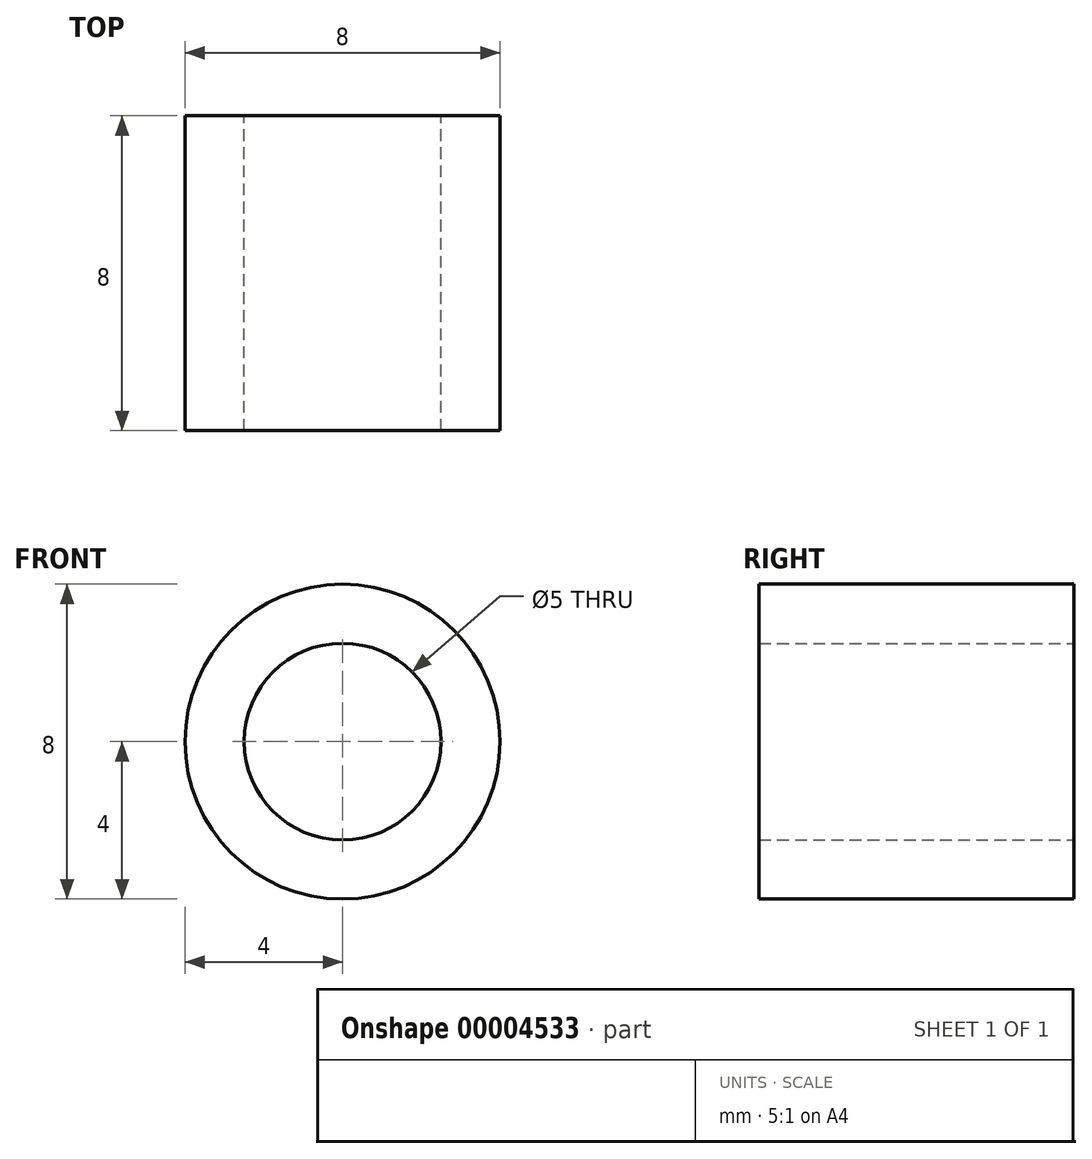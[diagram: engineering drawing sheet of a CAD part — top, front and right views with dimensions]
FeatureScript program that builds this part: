
annotation { "Feature Type Name" : "Feature", "Feature Type Description" : "" }
export const myFeature = defineFeature(function(context is Context, id is Id, definition is map)
    precondition{}
    {
        {
            var Q0;
            Q0=qCreatedBy(makeId("Front.planeOp"),FACE);
            var sketch = newSketch(context, id + "F0", { "sketchPlane" : qUnion([Q0])});
            skCircle(sketch, "E0", {"center": v(0, 0) * mm, "radius": 4 * mm});
            skCircle(sketch, "E1", {"center": v(0, 0) * mm, "radius": 2.5 * mm});
            skSolve(sketch);
        }
        {
            var Q0;
            Q0=makeQuery(id+"F0.imprint","IMPRINT",FACE,{"disambiguationData":[TD([[makeQuery(id+"F0.imprint","IMPRINT",EDGE,{"derivedFrom":sQuery(id+"F0.wireOp",EDGE,"E0")}),1.0]])]});
            extrude(context, id + "F1", {"entities" : qUnion([Q0]), "depth" : 8 * mm});
        }
    });
